# Revit family: RAV_GM1AT8_224-280_Outdoor Unit
name_source: partatom
category: Mechanical Equipment
revit_build: Autodesk Revit 2017 (Build: 20160225_1515(x64)
units: mm (PartAtom-declared; Revit-internal decimal feet)

## family parameters
Always vertical = Yes
Cut with Voids When Loaded = No
OmniClass Number = 23.75.00.00
OmniClass Title = Climate Control (HVAC)
Part Type = Normal
Room Calculation Point = No
Round Connector Dimension = Use Diameter
Shared = No
Work Plane-Based = No

## types (2) — shared parameters
Article Description = R32 Big DI  3PH
Compressor detail - Motor output  (kW) = -
Compressor detail - Type = Hermetic DC twin rotary compressor
Content Supplier URL = www.hcltech.com
Custom = No
Depth (mm) = 370 mm  [stored 1.21391 ft]
Description = R32 Big DI  3PH
Drain pipe(mm) = -
Duct diameters(mm) = -
EMCS = 4
ETIM Article Class = EC001213
Energy class-Cooling/Heating = -
Frequency (Hz) = -
Height (mm) = 1550 mm  [stored 5.0853 ft]
MCA (A) = -
MEPcontent Class = HEATPUMP
MOCP (A) = 25
Manufacturer = Toshiba
Manufacturer URL = https://www.toshiba-carrier.co.jp
Operating range - Cooling (°C) = -15 - 46
Pdesigh-Cooling/Heating = -
Piping diameter (mm)-Gas = 29 mm
Piping diameter (mm)-Liquid = 13 mm
Power consumption-Cooling = -
Power consumption-Heating = -
Rated Power Consumption kW-Cooling/Heating = -
Rated efficiency-EER / COP = -
Red = Colour RGB-250 000 000
Refrigerant information = -
Running current-Cooling = -
Running current-Heating = -
Seasonal Efficiency-SEER  / SCOP = -
Sound pressure - Cooling/Heating (dB)-Low = -
Sound pressure - Cooling/Heating (dB)-Low+ = -
Sound pressure - Cooling/Heating (dB)-Mid = -
Sound pressure - Cooling/Heating (dB)-Mid+ = -
Top  Clearance (mm) = 1000 mm  [stored 3.28084 ft]
URL = https://www.toshiba-carrier.co.jp
Voltage (V) = -
Weight (Kg) = 142
White = Colour RGB-255 255 255
Width (mm) = 1010 mm  [stored 3.31365 ft]

## per-type parameters (varying)
| type | Airflow m3/h-Cooling/Heating | Maximum current | Operating range - Heating (°C) | Rated Capacity kW-Cooling/Heating | Sound pressure - Cooling/Heating (dB)-High | Static pressure |
| RAV-GM2241AT8-E | 9150 | 18.0 | -20 -15 | 20.0 / 22.4 | 58 / 60 | - |
| RAV-GM2801AT8-E | 10890 | 23 | -20 - 15 | 23.5 / 27.0 | 61 / 63 |  |

note: column(s) folded — value = type name in every type: Article Type, Manufacturer Art. No., Model

note: [stored X ft] marks values corroborated as IEEE doubles in the binary element streams (Revit-internal decimal feet)

## geometry (parser evidence)
native form markers: Sweep x8
no freeform markers — native parametric forms only
